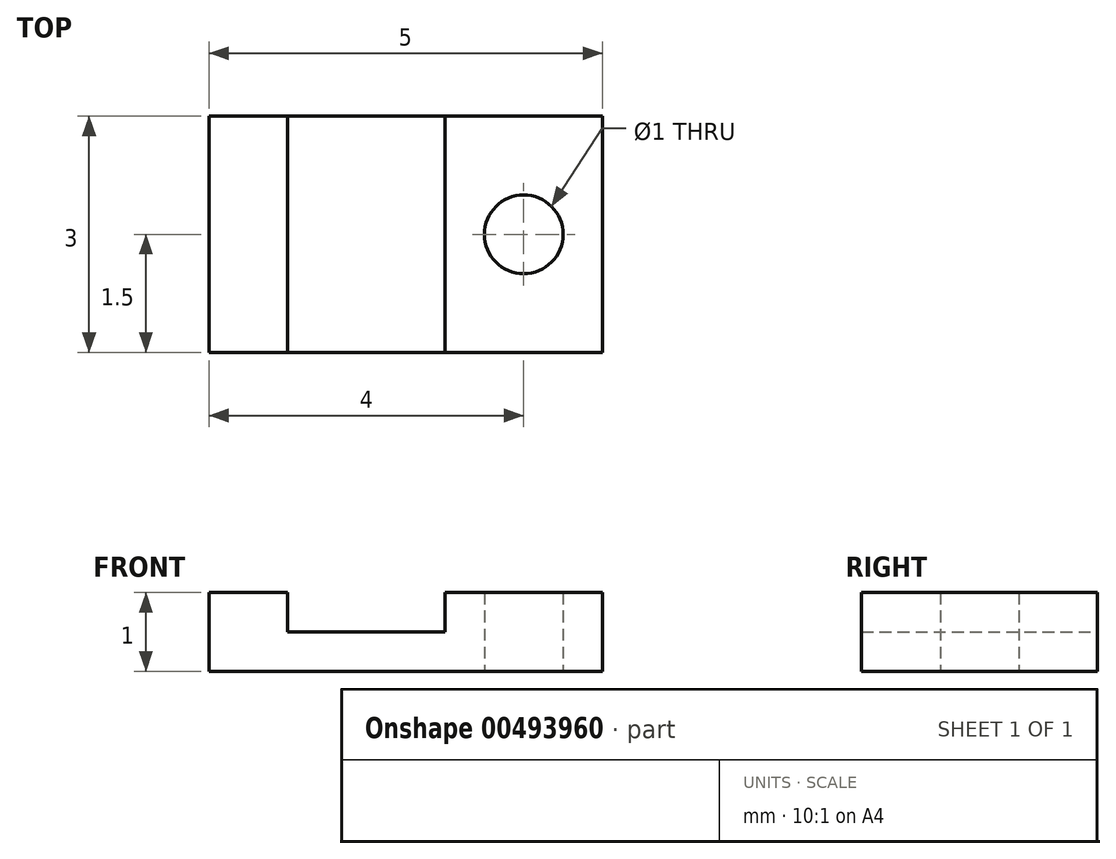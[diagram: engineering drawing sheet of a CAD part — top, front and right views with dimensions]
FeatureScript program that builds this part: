
annotation { "Feature Type Name" : "Feature", "Feature Type Description" : "" }
export const myFeature = defineFeature(function(context is Context, id is Id, definition is map)
    precondition{}
    {
        {
            var Q0;
            Q0=qCreatedBy(makeId("Top.planeOp"),FACE);
            var sketch = newSketch(context, id + "F0", { "sketchPlane" : qUnion([Q0])});
            skLineSegment(sketch, "E0", {"start": v(0, 0) * mm, "end": v(0, 3) * mm});
            skLineSegment(sketch, "E1", {"start": v(0, 3) * mm, "end": v(-2, 3) * mm});
            skLineSegment(sketch, "E2", {"start": v(-2, 3) * mm, "end": v(-4, 3) * mm});
            skLineSegment(sketch, "E3", {"start": v(-4, 3) * mm, "end": v(-5, 3) * mm});
            skLineSegment(sketch, "E4", {"start": v(-5, 3) * mm, "end": v(-5, 0) * mm});
            skLineSegment(sketch, "E5", {"start": v(-5, 0) * mm, "end": v(-4, 0) * mm});
            skLineSegment(sketch, "E6", {"start": v(-4, 0) * mm, "end": v(-2, 0) * mm});
            skLineSegment(sketch, "E7", {"start": v(-2, 0) * mm, "end": v(0, 0) * mm});
            skCircle(sketch, "E8", {"center": v(-1, 1.5) * mm, "radius": 0.5 * mm});
            skPoint(sketch, "E8.centerSnap0", {"position": v(0, 1.5) * mm});
            skLineSegment(sketch, "E9", {"start": v(-2, 3) * mm, "end": v(-2, 0) * mm});
            skLineSegment(sketch, "E10", {"start": v(-4, 0) * mm, "end": v(-4, 3) * mm});
            skSolve(sketch);
        }
        {
            var Q0;
            Q0=makeQuery(id+"F0.imprint","IMPRINT",FACE,{"disambiguationData":[TD([[makeQuery(id+"F0.imprint","IMPRINT",EDGE,{"derivedFrom":sQuery(id+"F0.wireOp",EDGE,"E3")}),1.0]])]});
            extrude(context, id + "F1", {"entities" : qUnion([Q0]), "depth" : 1 * mm});
        }
        {
            var Q0;
            Q0=makeQuery(id+"F0.imprint","IMPRINT",FACE,{"disambiguationData":[TD([[makeQuery(id+"F0.imprint","IMPRINT",EDGE,{"derivedFrom":sQuery(id+"F0.wireOp",EDGE,"E2")}),1.0]])]});
            extrude(context, id + "F2", {"entities" : qUnion([Q0]), "operationType" : NewBodyOperationType.ADD, "depth" : .5 * mm});
        }
        {
            var Q0;
            Q0=makeQuery(id+"F0.imprint","IMPRINT",FACE,{"disambiguationData":[TD([[makeQuery(id+"F0.imprint","IMPRINT",EDGE,{"derivedFrom":sQuery(id+"F0.wireOp",EDGE,"E0")}),1.0]])]});
            extrude(context, id + "F3", {"entities" : qUnion([Q0]), "operationType" : NewBodyOperationType.ADD, "depth" : 1 * mm});
        }
    });
